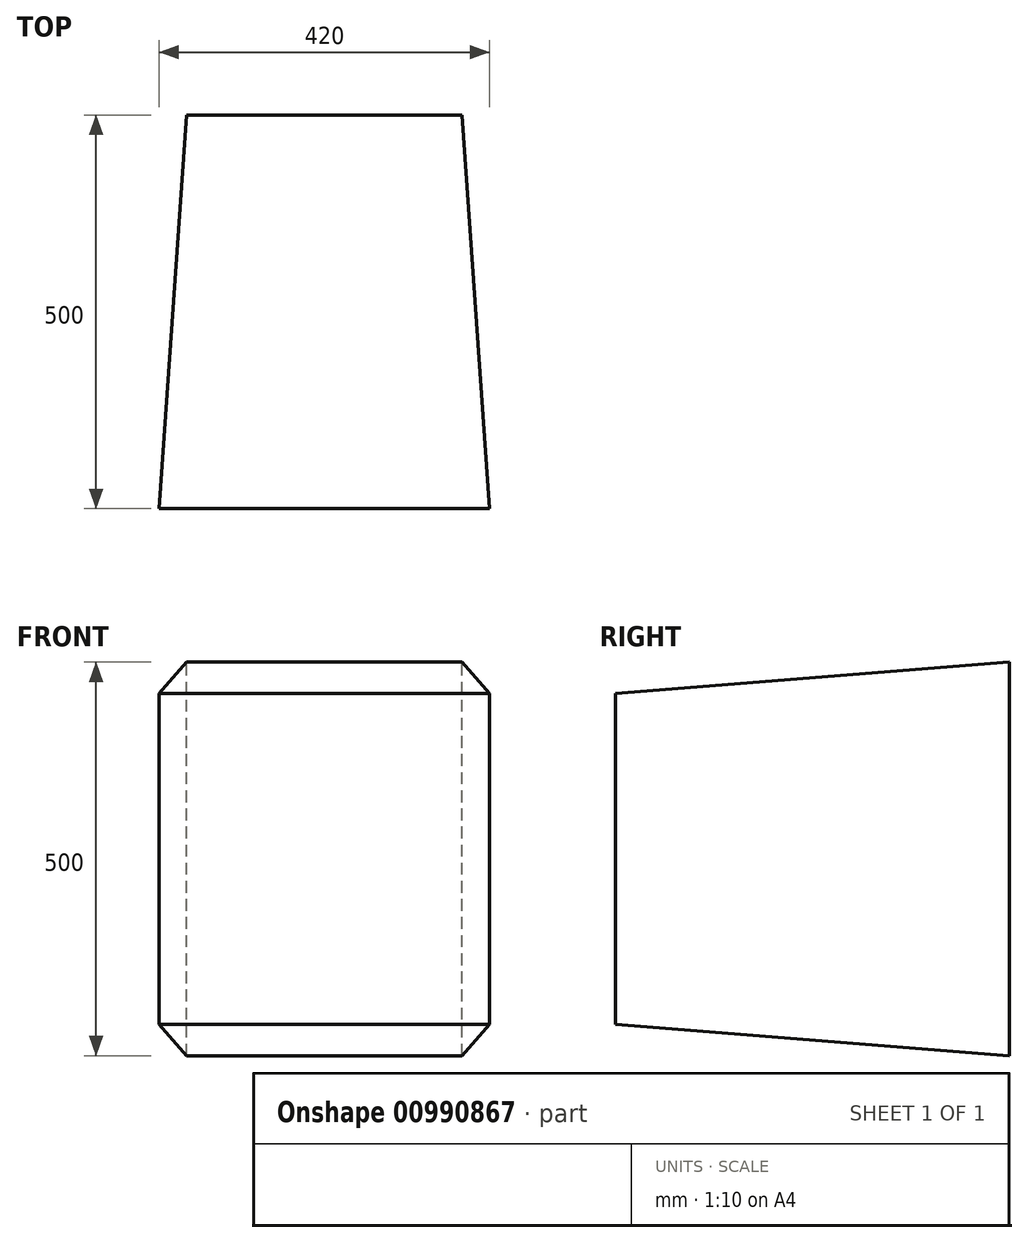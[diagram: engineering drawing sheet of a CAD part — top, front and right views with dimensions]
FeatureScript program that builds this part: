
annotation { "Feature Type Name" : "Feature", "Feature Type Description" : "" }
export const myFeature = defineFeature(function(context is Context, id is Id, definition is map)
    precondition{}
    {
        {
            var Q0;
            Q0=qCreatedBy(makeId("Front.planeOp"),FACE);
            var sketch = newSketch(context, id + "F0", { "sketchPlane" : qUnion([Q0])});
            skLineSegment(sketch, "E0.bottom", {"start": v(0, 0) * mm, "end": v(350, 0) * mm});
            skLineSegment(sketch, "E0.top", {"start": v(0, 500) * mm, "end": v(350, 500) * mm});
            skLineSegment(sketch, "E0.left", {"start": v(0, 0) * mm, "end": v(0, 500) * mm});
            skLineSegment(sketch, "E0.right", {"start": v(350, 0) * mm, "end": v(350, 500) * mm});
            skSolve(sketch);
        }
        {
            var Q0;
            Q0=qCreatedBy(makeId("Front.planeOp"),FACE);
            cPlane(context, id + "F1", {"entities" : qUnion([Q0]), "cplaneType" : CPlaneType.OFFSET, "offset" : 500 * mm, "width" : 150 * mm, "height" : 150 * mm});
        }
        {
            var Q0;
            Q0=qCreatedBy(id+"F1.planeOp",FACE);
            var sketch = newSketch(context, id + "F2", { "sketchPlane" : qUnion([Q0])});
            skLineSegment(sketch, "E1", {"start": v(-35, 40) * mm, "end": v(385, 40) * mm});
            skLineSegment(sketch, "E2", {"start": v(-35, 40) * mm, "end": v(-35, 460) * mm});
            skLineSegment(sketch, "E3", {"start": v(-35, 460) * mm, "end": v(385, 460) * mm});
            skLineSegment(sketch, "E4", {"start": v(385, 460) * mm, "end": v(385, 40) * mm});
            skSolve(sketch);
        }
        {
            var Q0;
            Q0=makeQuery(id+"F0.imprint","IMPRINT",FACE,{"disambiguationData":[TD([[makeQuery(id+"F0.imprint","IMPRINT",EDGE,{"derivedFrom":sQuery(id+"F0.wireOp",EDGE,"E0.bottom")}),1.0]])]});
            var Q1;
            Q1=makeQuery(id+"F2.imprint","IMPRINT",FACE,{"disambiguationData":[TD([[makeQuery(id+"F2.imprint","IMPRINT",EDGE,{"derivedFrom":sQuery(id+"F2.wireOp",EDGE,"E1")}),1.0]])]});
            loft(context, id + "F3", {"sheetProfilesArray" : [{ "sheetProfileEntities" : qUnion([Q0]) }, { "sheetProfileEntities" : qUnion([Q1]) }]});
        }
    });
